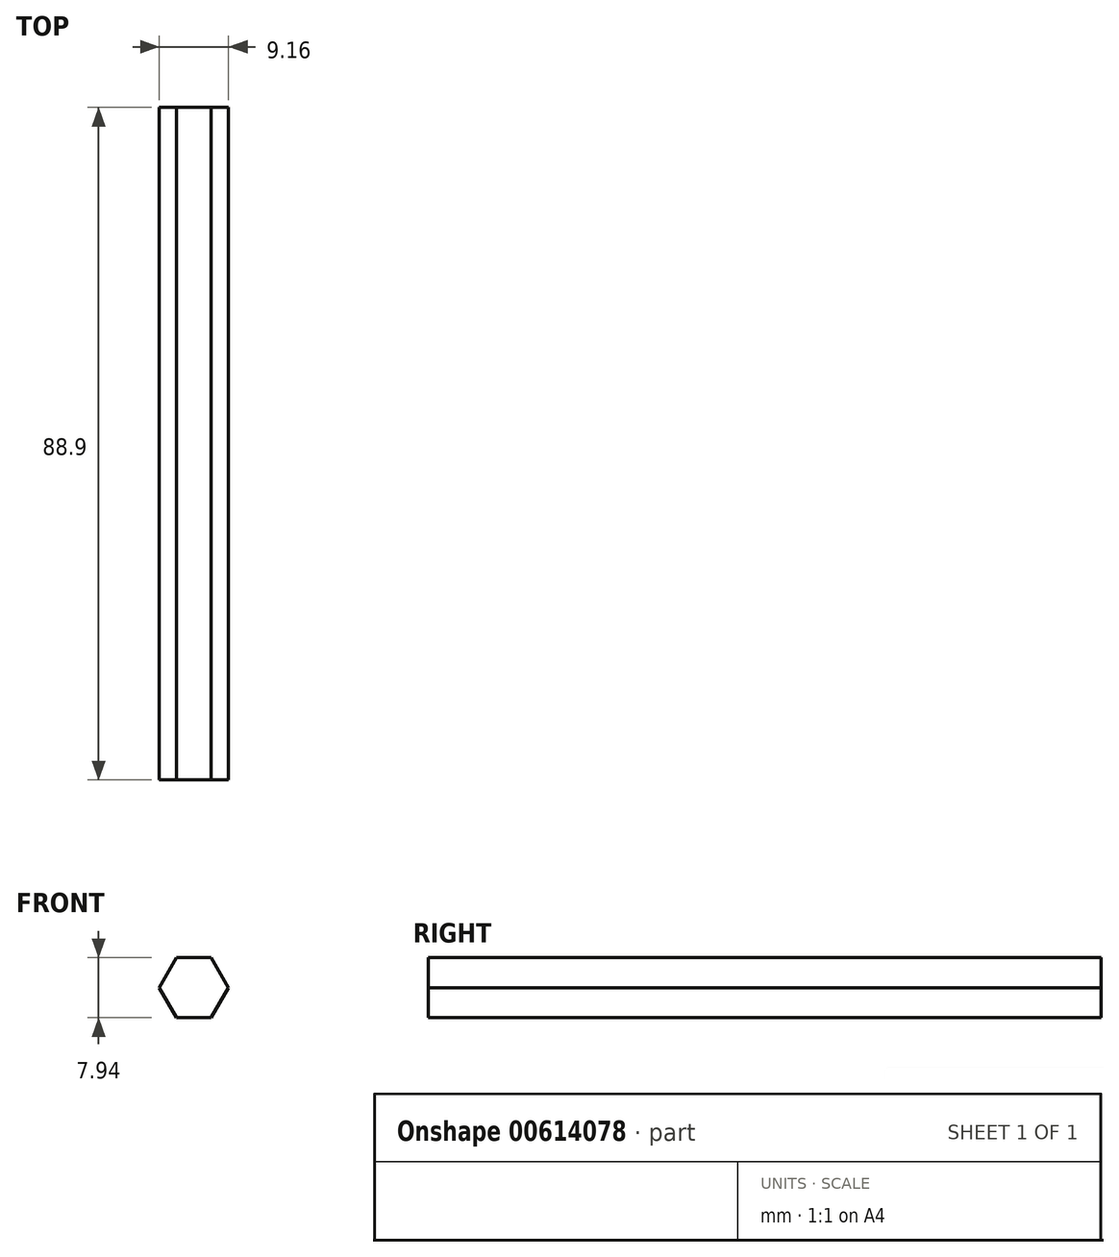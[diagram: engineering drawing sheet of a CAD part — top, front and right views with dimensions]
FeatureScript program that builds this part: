
annotation { "Feature Type Name" : "Feature", "Feature Type Description" : "" }
export const myFeature = defineFeature(function(context is Context, id is Id, definition is map)
    precondition{}
    {
        {
            var Q0;
            Q0=qCreatedBy(makeId("Front.planeOp"),FACE);
            var sketch = newSketch(context, id + "F0", { "sketchPlane" : qUnion([Q0])});
            skCircle(sketch, "E0.cCircle", {"center": v(0, 0) * mm, "radius": 3.97 * mm, "construction": true});
            skLineSegment(sketch, "E0.0", {"start": v(2.3, -3.97) * mm, "end": v(-2.3, -3.97) * mm});
            skLineSegment(sketch, "E0.1", {"start": v(-2.3, -3.97) * mm, "end": v(-4.58, 0) * mm});
            skLineSegment(sketch, "E0.2", {"start": v(-4.58, 0) * mm, "end": v(-2.3, 3.97) * mm});
            skLineSegment(sketch, "E0.3", {"start": v(-2.3, 3.97) * mm, "end": v(2.3, 3.97) * mm});
            skLineSegment(sketch, "E0.4", {"start": v(2.3, 3.97) * mm, "end": v(4.58, 0) * mm});
            skLineSegment(sketch, "E0.5", {"start": v(4.58, 0) * mm, "end": v(2.3, -3.97) * mm});
            skPoint(sketch, "E0.0.midPoint", {"position": v(0, -3.97) * mm});
            skSolve(sketch);
        }
        {
            var Q0;
            Q0=makeQuery(id+"F0.imprint","IMPRINT",FACE,{"disambiguationData":[TD([[makeQuery(id+"F0.imprint","IMPRINT",EDGE,{"derivedFrom":sQuery(id+"F0.wireOp",EDGE,"E0.0")}),-1.0]])]});
            extrude(context, id + "F1", {"entities" : qUnion([Q0]), "endBound" : BoundingType.SYMMETRIC, "depth" : 88.9 * mm, "offsetDistance" : 25.4 * mm});
        }
    });
